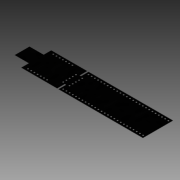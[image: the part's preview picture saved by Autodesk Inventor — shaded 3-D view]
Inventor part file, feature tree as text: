
AUTODESK INVENTOR PART (.ipt)
format: ipt  version: 2016 SP1 (Build 200210100, 210)  size: 2,507,776 bytes
history: native  units: mm
features: extrude x5, pattern_linear x3, mirror x3, plane x2, fillet x2, sketch x1, other x1
ambient origin geometry x8: Origin, YZ Plane, XZ Plane, XY Plane, X Axis, Y Axis, Z Axis, Center Point
bodies: Solid1 (feature_tree)
feature tree (17):
  sketch  "Sketch1"  dims[d0=11.99mm d1=11.35mm d2=24.13mm d3=97.54mm d23=70.0mm d25=2.57mm d26=10.0mm d28=10.0mm d31=1.0mm d32=260.0mm d34=2.56mm d35=10.0mm d37=10.0mm d40=1.0mm d41=50.0mm d43=2.55mm d44=10.0mm d46=10.0mm d49=0.0787mm d50=0.0mm d52=0.0787mm d53=0.0mm d54=70.0mm d56=2.55mm d57=0.0787mm d58=0.0mm d59=260.0mm d61=2.56mm d62=0.0787mm d63=0.0mm d64=50.0mm d66=2.55mm d67=6.5mm d68=0.0787mm d69=0.0mm d70=0.05mm d71=0.05mm]
  extrude  "Extrusion1"  Depth=11.35mm
  extrude  "Extrusion2"  Depth=24.13mm
  pattern_linear  "Rectangular Pattern1"  Spacing1=97.54mm  [1 undecoded]
  extrude  "Extrusion3"  Depth=10.0mm
  pattern_linear  "Rectangular Pattern2"  Spacing1=1.0mm  [1 undecoded]
  plane  "Work Plane1"
  mirror  "Mirror1"
  extrude  "Extrusion4"  Depth=10.0mm
  pattern_linear  "Rectangular Pattern3"  Spacing1=1.0mm  [1 undecoded]
  extrude  "Extrusion5"  Depth=10.0mm
  fillet  "Fillet1"  Radius=0.0787mm
  mirror  "Mirror2"
  plane  "Work Plane2"
  mirror  "Mirror3"
  fillet  "Fillet2"  Radius=0.0787mm
  other  "Image1"
note: 3 required parameter values undecoded (feature->parameter linkage not recoverable at this tier; creation-order binding heuristic only, values carry confidence <= 0.55)
